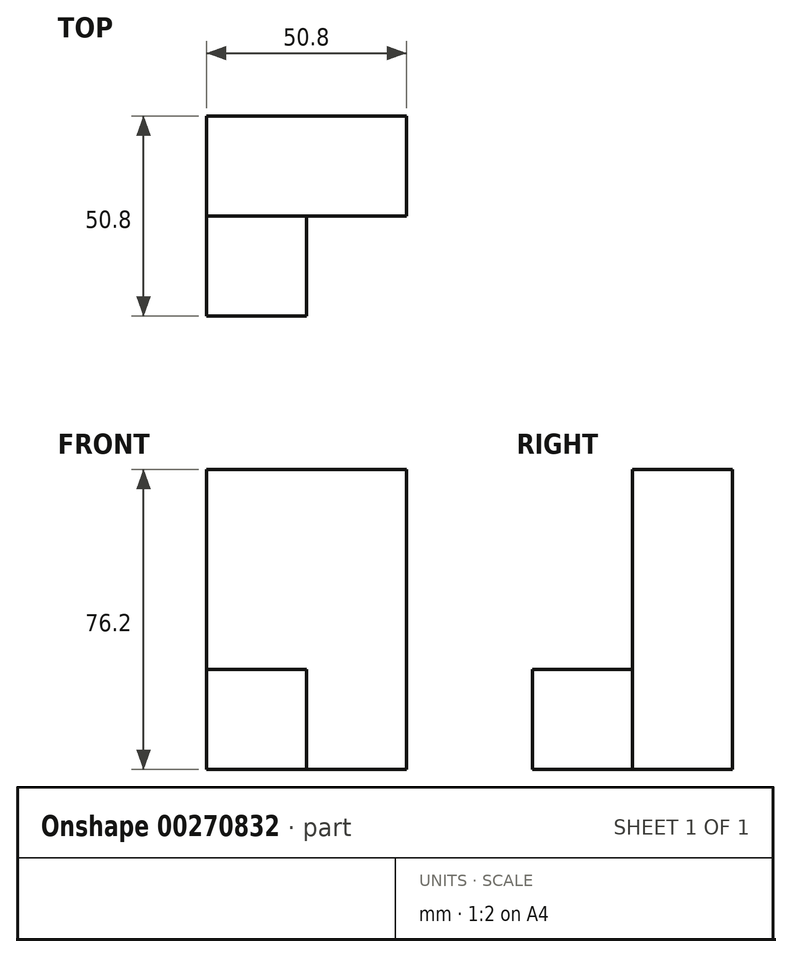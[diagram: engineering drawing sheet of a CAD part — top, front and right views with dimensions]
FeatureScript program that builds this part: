
annotation { "Feature Type Name" : "Feature", "Feature Type Description" : "" }
export const myFeature = defineFeature(function(context is Context, id is Id, definition is map)
    precondition{}
    {
        {
            var Q0;
            Q0=qCreatedBy(makeId("Front.planeOp"),FACE);
            var sketch = newSketch(context, id + "F0", { "sketchPlane" : qUnion([Q0])});
            skLineSegment(sketch, "E0.bottom", {"start": v(0, 0) * mm, "end": v(-50.8, 0) * mm});
            skLineSegment(sketch, "E0.top", {"start": v(0, 76.2) * mm, "end": v(-50.8, 76.2) * mm});
            skLineSegment(sketch, "E0.left", {"start": v(0, 0) * mm, "end": v(0, 76.2) * mm});
            skLineSegment(sketch, "E0.right", {"start": v(-50.8, 0) * mm, "end": v(-50.8, 76.2) * mm});
            skLineSegment(sketch, "E1.bottom", {"start": v(5.73, 25.2) * mm, "end": v(7.26, 25.2) * mm});
            skLineSegment(sketch, "E1.top", {"start": v(5.73, 25.2) * mm, "end": v(7.26, 25.2) * mm});
            skLineSegment(sketch, "E1.left", {"start": v(5.73, 25.2) * mm, "end": v(5.73, 25.2) * mm});
            skLineSegment(sketch, "E1.right", {"start": v(7.26, 25.2) * mm, "end": v(7.26, 25.2) * mm});
            skSolve(sketch);
        }
        {
            var Q0;
            Q0 = qSketchRegion(id + "F0", true);
            extrude(context, id + "F1", {"entities" : qUnion([Q0]), "depth" : 25.4 * mm});
        }
        {
            var Q0;
            Q0=makeQuery(id+"F1.opExtrude","CAP_FACE",FACE,{"disambiguationData":[OSD([sQuery(id+"F0.wireOp",EDGE,"E0.bottom"),sQuery(id+"F0.wireOp",EDGE,"E0.top"),sQuery(id+"F0.wireOp",EDGE,"E0.left"),sQuery(id+"F0.wireOp",EDGE,"E0.right")])],"isStart":false});
            var sketch = newSketch(context, id + "F2", { "sketchPlane" : qUnion([Q0])});
            skLineSegment(sketch, "E2.bottom", {"start": v(-50.8, 0) * mm, "end": v(-25.4, 0) * mm});
            skLineSegment(sketch, "E2.top", {"start": v(-50.8, 25.4) * mm, "end": v(-25.4, 25.4) * mm});
            skLineSegment(sketch, "E2.left", {"start": v(-50.8, 0) * mm, "end": v(-50.8, 25.4) * mm});
            skLineSegment(sketch, "E2.right", {"start": v(-25.4, 0) * mm, "end": v(-25.4, 25.4) * mm});
            skSolve(sketch);
        }
        {
            var Q0;
            Q0 = qSketchRegion(id + "F2", true);
            extrude(context, id + "F3", {"entities" : qUnion([Q0]), "operationType" : NewBodyOperationType.ADD, "depth" : 25.4 * mm});
        }
    });
